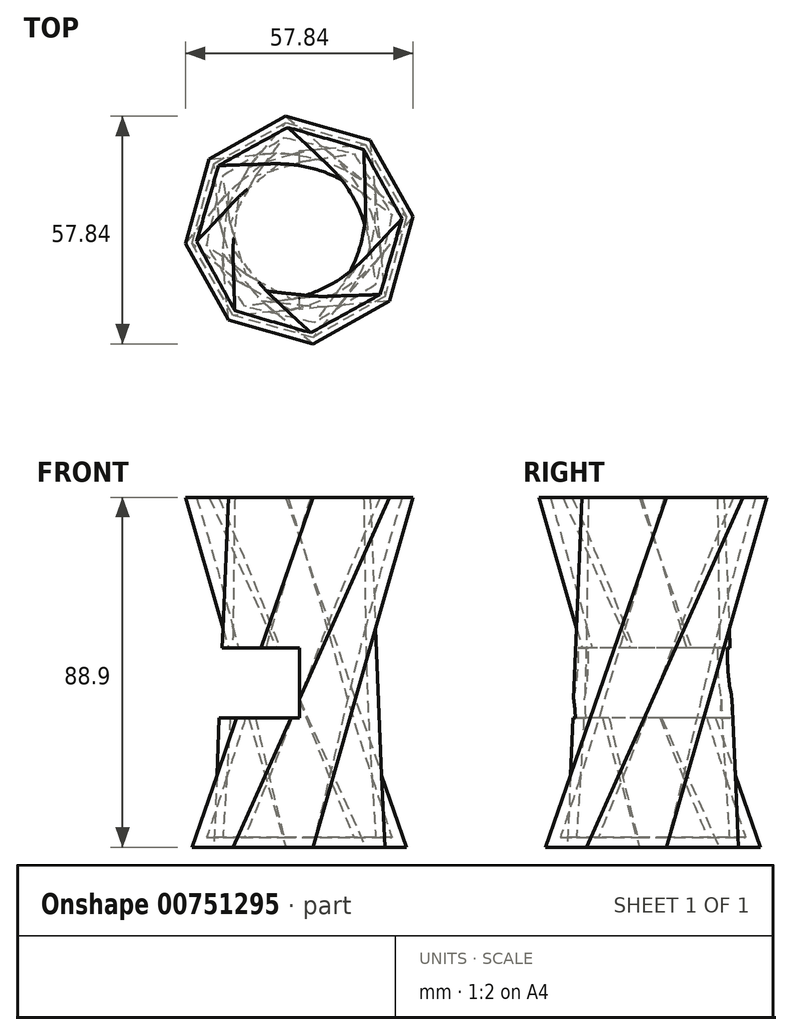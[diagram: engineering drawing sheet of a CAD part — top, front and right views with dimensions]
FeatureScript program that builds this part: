
annotation { "Feature Type Name" : "Feature", "Feature Type Description" : "" }
export const myFeature = defineFeature(function(context is Context, id is Id, definition is map)
    precondition{}
    {
        {
            var Q0;
            Q0=qCreatedBy(makeId("Top.planeOp"),FACE);
            var sketch = newSketch(context, id + "F0", { "sketchPlane" : qUnion([Q0])});
            skCircle(sketch, "E0.cCircle", {"center": v(0, 0) * mm, "radius": 25.4 * mm, "construction": true});
            skLineSegment(sketch, "E0.0", {"start": v(-21.71, 16.87) * mm, "end": v(-3.42, 27.28) * mm});
            skLineSegment(sketch, "E0.1", {"start": v(-3.42, 27.28) * mm, "end": v(16.87, 21.71) * mm});
            skLineSegment(sketch, "E0.2", {"start": v(16.87, 21.71) * mm, "end": v(27.28, 3.42) * mm});
            skLineSegment(sketch, "E0.3", {"start": v(27.28, 3.42) * mm, "end": v(21.71, -16.87) * mm});
            skLineSegment(sketch, "E0.4", {"start": v(21.71, -16.87) * mm, "end": v(3.42, -27.28) * mm});
            skLineSegment(sketch, "E0.5", {"start": v(3.42, -27.28) * mm, "end": v(-16.87, -21.71) * mm});
            skLineSegment(sketch, "E0.6", {"start": v(-16.87, -21.71) * mm, "end": v(-27.28, -3.42) * mm});
            skLineSegment(sketch, "E0.7", {"start": v(-27.28, -3.42) * mm, "end": v(-21.71, 16.87) * mm});
            skPoint(sketch, "E0.0.midPoint", {"position": v(-12.57, 22.07) * mm});
            skSolve(sketch);
        }
        {
            var Q0;
            Q0=makeQuery(id+"F0.imprint","IMPRINT",FACE,{"disambiguationData":[TD([[makeQuery(id+"F0.imprint","IMPRINT",EDGE,{"derivedFrom":sQuery(id+"F0.wireOp",EDGE,"E0.0")}),-1.0]])]});
            cPlane(context, id + "F1", {"entities" : qUnion([Q0]), "cplaneType" : CPlaneType.OFFSET, "offset" : 88.9 * mm, "width" : 152.4 * mm, "height" : 152.4 * mm});
        }
        {
            var Q0;
            Q0=qCreatedBy(id+"F1.planeOp",FACE);
            var sketch = newSketch(context, id + "F2", { "sketchPlane" : qUnion([Q0])});
            skCircle(sketch, "E1.cCircle", {"center": v(0, 0) * mm, "radius": 26.91 * mm, "construction": true});
            skLineSegment(sketch, "E1.0", {"start": v(-22.9, 18) * mm, "end": v(-3.47, 28.92) * mm});
            skLineSegment(sketch, "E1.1", {"start": v(-3.47, 28.92) * mm, "end": v(18, 22.9) * mm});
            skLineSegment(sketch, "E1.2", {"start": v(18, 22.9) * mm, "end": v(28.92, 3.47) * mm});
            skLineSegment(sketch, "E1.3", {"start": v(28.92, 3.47) * mm, "end": v(22.9, -18) * mm});
            skLineSegment(sketch, "E1.4", {"start": v(22.9, -18) * mm, "end": v(3.47, -28.92) * mm});
            skLineSegment(sketch, "E1.5", {"start": v(3.47, -28.92) * mm, "end": v(-18, -22.9) * mm});
            skLineSegment(sketch, "E1.6", {"start": v(-18, -22.9) * mm, "end": v(-28.92, -3.47) * mm});
            skLineSegment(sketch, "E1.7", {"start": v(-28.92, -3.47) * mm, "end": v(-22.9, 18) * mm});
            skPoint(sketch, "E1.0.midPoint", {"position": v(-13.19, 23.46) * mm});
            skSolve(sketch);
        }
        {
            var Q0;
            Q0=makeQuery(id+"F2.imprint","IMPRINT",FACE,{"disambiguationData":[TD([[makeQuery(id+"F2.imprint","IMPRINT",EDGE,{"derivedFrom":sQuery(id+"F2.wireOp",EDGE,"E1.0")}),-1.0]])]});
            var Q1;
            Q1=makeQuery(id+"F0.imprint","IMPRINT",FACE,{"disambiguationData":[TD([[makeQuery(id+"F0.imprint","IMPRINT",EDGE,{"derivedFrom":sQuery(id+"F0.wireOp",EDGE,"E0.0")}),-1.0]])]});
            var Q2;
            Q2=sQuery(id+"F2.wireOp",VERTEX,"E1.7.start");
            var Q3;
            Q3=sQuery(id+"F0.wireOp",VERTEX,"E0.1.start");
            loft(context, id + "F3", {"sheetProfilesArray" : [{ "sheetProfileEntities" : qUnion([Q0]) }, { "sheetProfileEntities" : qUnion([Q1]) }], "matchConnections" : true, "connections" : [{ "connectionEntities" : qUnion([Q2, Q3]), "connectionEdgeQueries" : qUnion([]), "connectionEdgeParameters" : [] }]});
        }
        {
            var Q0;
            Q0=makeQuery(id+"F3.opLoft","CAP_FACE",FACE,{"disambiguationData":[OSD([makeQuery(id+"F2.imprint","IMPRINT",FACE,{"disambiguationData":[TD([[makeQuery(id+"F2.imprint","IMPRINT",EDGE,{"derivedFrom":sQuery(id+"F2.wireOp",EDGE,"E1.0")}),-1.0]])]})])],"isStart":true});
            shell(context, id + "F4", {"entities" : qUnion([Q0]), "thickness" : 2.54 * mm});
        }
        {
            var Q0;
            Q0=qCreatedBy(makeId("Right.planeOp"),FACE);
            var sketch = newSketch(context, id + "F5", { "sketchPlane" : qUnion([Q0])});
            skLineSegment(sketch, "E2.bottom", {"start": v(50.14, 207.02) * mm, "end": v(32.62, 207.02) * mm});
            skLineSegment(sketch, "E2.top", {"start": v(50.14, 207.74) * mm, "end": v(32.62, 207.74) * mm});
            skLineSegment(sketch, "E2.left", {"start": v(50.14, 207.02) * mm, "end": v(50.14, 207.74) * mm});
            skLineSegment(sketch, "E2.right", {"start": v(32.62, 207.02) * mm, "end": v(32.62, 207.74) * mm});
            skLineSegment(sketch, "E3.bottom", {"start": v(-38.76, 50.64) * mm, "end": v(50.14, 50.64) * mm});
            skLineSegment(sketch, "E3.top", {"start": v(-38.76, 32.86) * mm, "end": v(50.14, 32.86) * mm});
            skLineSegment(sketch, "E3.left", {"start": v(-38.76, 50.64) * mm, "end": v(-38.76, 32.86) * mm});
            skLineSegment(sketch, "E3.right", {"start": v(50.14, 50.64) * mm, "end": v(50.14, 32.86) * mm});
            skSolve(sketch);
        }
        {
            var Q0;
            Q0 = qSketchRegion(id + "F5", true);
            extrude(context, id + "F6", {"entities" : qUnion([Q0]), "operationType" : NewBodyOperationType.REMOVE, "oppositeDirection" : true, "depth" : 25.4 * mm, "offsetDistance" : 25.4 * mm});
        }
    });
